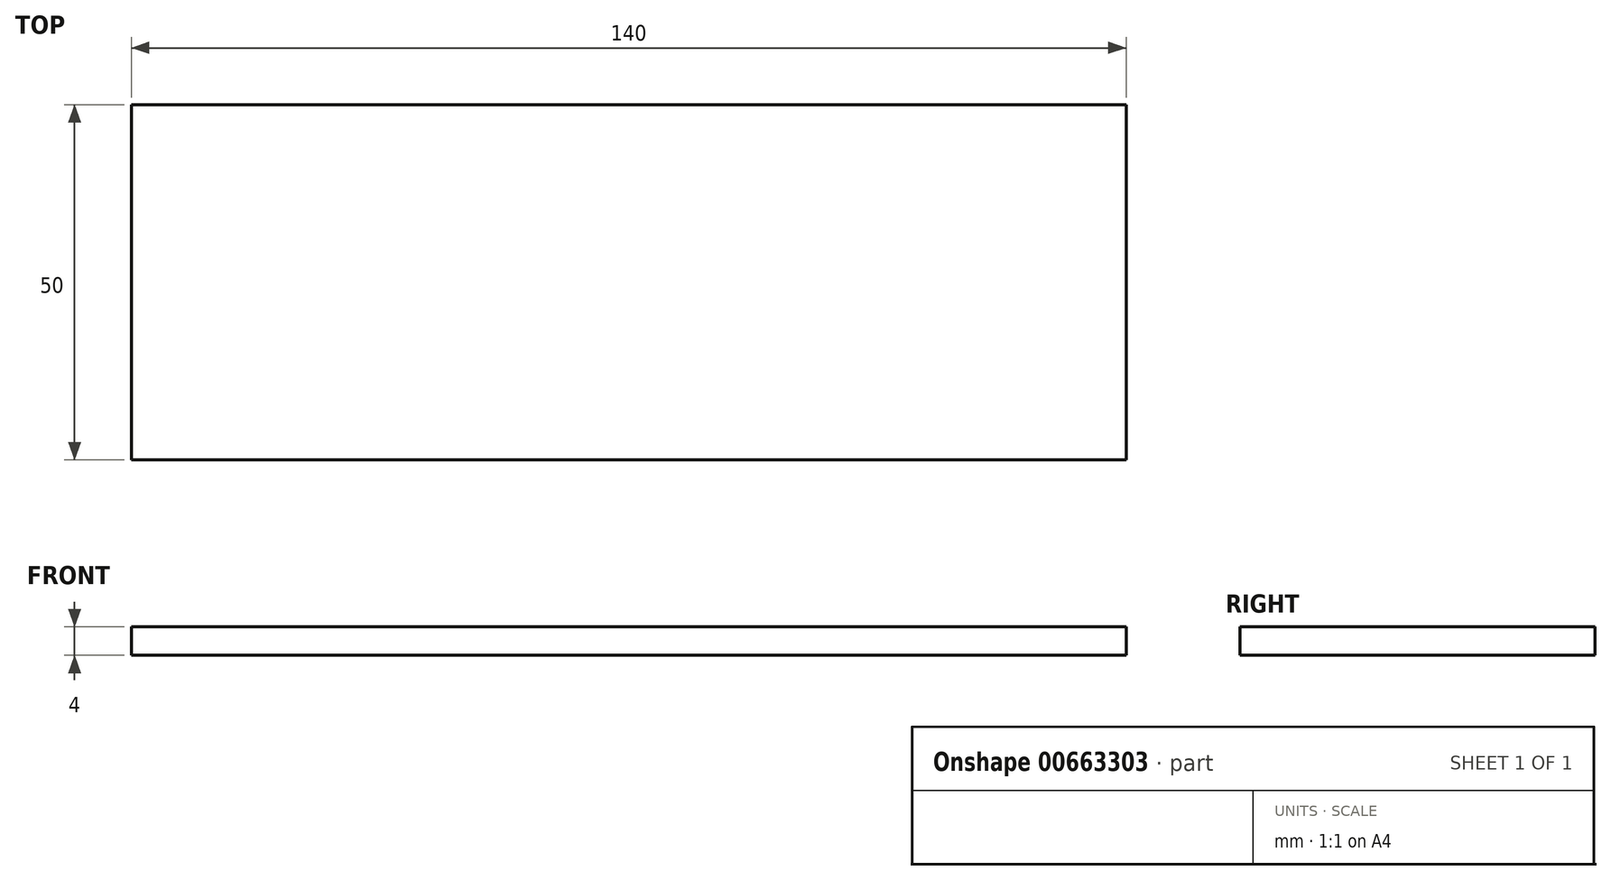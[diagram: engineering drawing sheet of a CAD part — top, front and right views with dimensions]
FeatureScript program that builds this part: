
annotation { "Feature Type Name" : "Feature", "Feature Type Description" : "" }
export const myFeature = defineFeature(function(context is Context, id is Id, definition is map)
    precondition{}
    {
        {
            var Q0;
            Q0=qCreatedBy(makeId("Top.planeOp"),FACE);
            var sketch = newSketch(context, id + "F0", { "sketchPlane" : qUnion([Q0])});
            skLineSegment(sketch, "E0.bottom", {"start": v(0, 0) * mm, "end": v(140, 0) * mm});
            skLineSegment(sketch, "E0.top", {"start": v(0, 50) * mm, "end": v(140, 50) * mm});
            skLineSegment(sketch, "E0.left", {"start": v(0, 0) * mm, "end": v(0, 50) * mm});
            skLineSegment(sketch, "E0.right", {"start": v(140, 0) * mm, "end": v(140, 50) * mm});
            skSolve(sketch);
        }
        {
            var Q0;
            Q0 = qSketchRegion(id + "F0", true);
            extrude(context, id + "F1", {"entities" : qUnion([Q0]), "depth" : 4 * mm, "offsetDistance" : 25 * mm});
        }
    });
